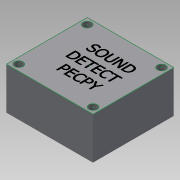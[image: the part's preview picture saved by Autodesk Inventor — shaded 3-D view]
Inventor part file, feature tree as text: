
AUTODESK INVENTOR PART (.ipt)
format: ipt  version: 2015 SP1 (Build 190203100, 203)  size: 97,280 bytes
history: native  units: mm
features: sketch x3, projected_geometry x2, extrude x1
ambient origin geometry x8: Origin, YZ Plane, XZ Plane, XY Plane, X Axis, Y Axis, Z Axis, Center Point
bodies: Solid1 (feature_tree)
feature tree (6):
  extrude  "Extrusion1"  Depth=28.81mm
  sketch  "Sketch2"  dims[d2=3.0mm]
  sketch  "Sketch3"  dims[d6=2.2mm d7=2.2mm d14=20.0mm d16=24.41mm d17=20.0mm d19=26.486mm d22=15.0mm d23=0.0mm]
  sketch  "Sketch1"  dims[d0=30.8864mm d1=28.81mm]
  projected_geometry  "Projected Loop1"
  projected_geometry  "Projected Loop2"
